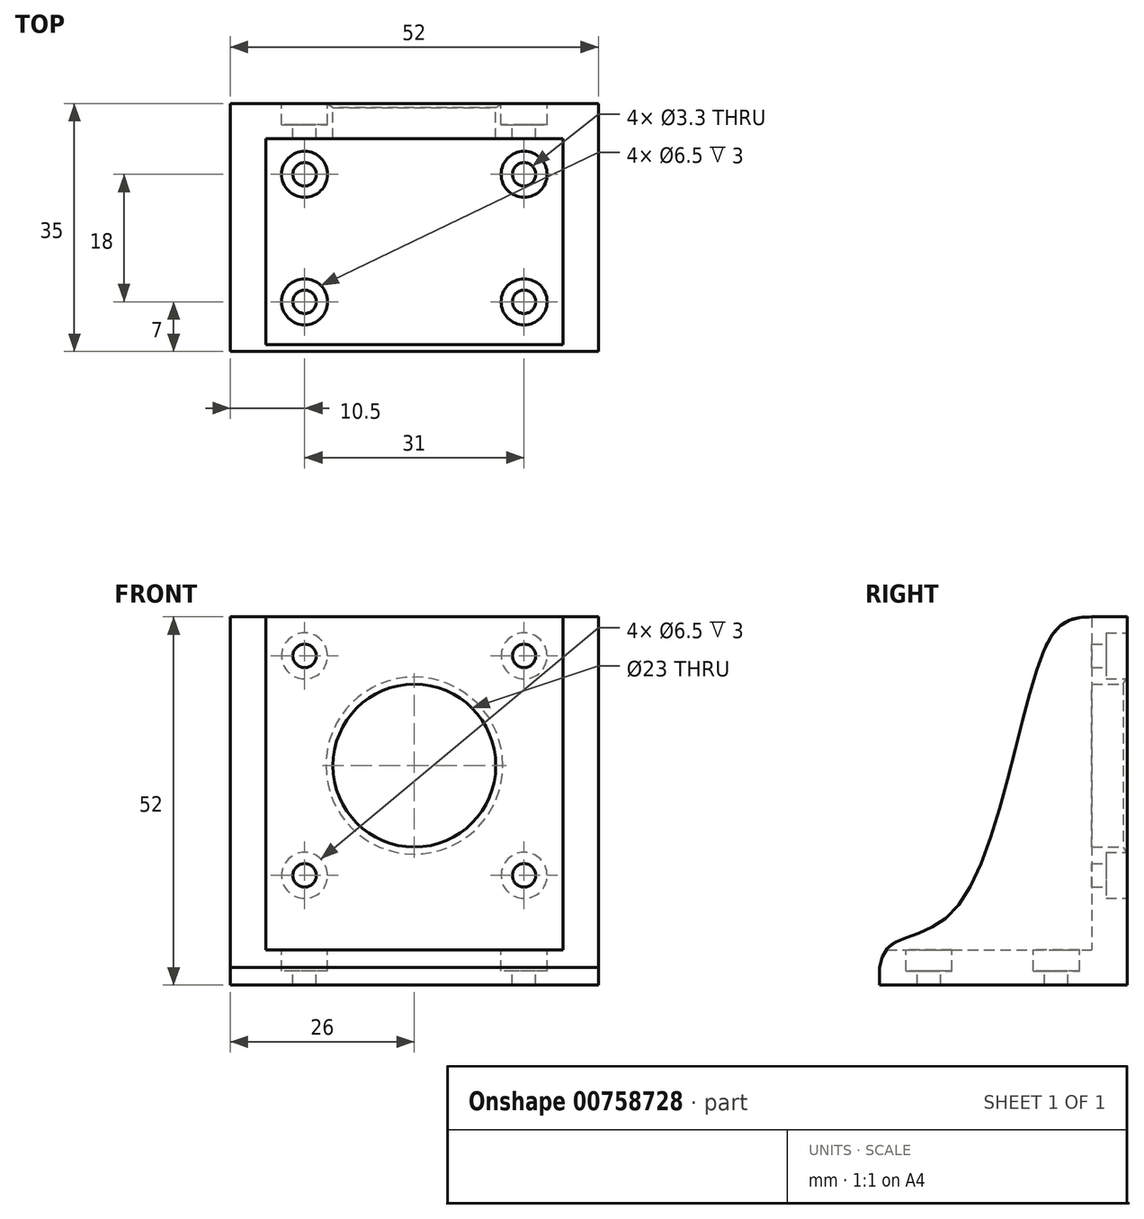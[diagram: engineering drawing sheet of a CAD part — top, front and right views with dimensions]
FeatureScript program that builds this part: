
annotation { "Feature Type Name" : "Feature", "Feature Type Description" : "" }
export const myFeature = defineFeature(function(context is Context, id is Id, definition is map)
    precondition{}
    {
        {
            var Q0;
            Q0=qCreatedBy(makeId("Front.planeOp"),FACE);
            var sketch = newSketch(context, id + "F0", { "sketchPlane" : qUnion([Q0])});
            skLineSegment(sketch, "E0.bottom", {"start": v(-26, 21) * mm, "end": v(0, 21) * mm});
            skLineSegment(sketch, "E0.top", {"start": v(-26, -31) * mm, "end": v(0, -31) * mm});
            skLineSegment(sketch, "E0.left", {"start": v(-26, 21) * mm, "end": v(-26, -31) * mm});
            skLineSegment(sketch, "E0.right", {"start": v(0, 21) * mm, "end": v(0, -31) * mm});
            skPoint(sketch, "E1", {"position": v(-15.5, 15.5) * mm});
            skPoint(sketch, "E2.MirrorP", {"position": v(-15.5, -15.5) * mm});
            skLineSegment(sketch, "E3.MirrorCS", {"start": v(-26, -21) * mm, "end": v(0, -21) * mm});
            skPoint(sketch, "E4", {"position": v(0, 0) * mm});
            skSolve(sketch);
        }
        {
            var Q0;
            Q0 = qSketchRegion(id + "F0", true);
            extrude(context, id + "F1", {"entities" : qUnion([Q0]), "depth" : 35 * mm, "offsetDistance" : 25 * mm});
        }
        {
            var Q0;
            Q0=makeQuery(id+"F1.opExtrude","SWEPT_FACE",FACE,{"disambiguationData":[OSD([sQuery(id+"F0.wireOp",EDGE,"E0.bottom")])]});
            var Q1;
            Q1=makeQuery(id+"F1.opExtrude","SWEPT_FACE",FACE,{"disambiguationData":[OSD([sQuery(id+"F0.wireOp",EDGE,"E0.right")])]});
            var Q2;
            Q2=makeQuery(id+"F1.opExtrude","CAP_FACE",FACE,{"disambiguationData":[OSD([sQuery(id+"F0.wireOp",EDGE,"E0.bottom"),sQuery(id+"F0.wireOp",EDGE,"E0.top"),sQuery(id+"F0.wireOp",EDGE,"E0.left"),sQuery(id+"F0.wireOp",EDGE,"E0.right")])],"isStart":false});
            shell(context, id + "F2", {"entities" : qUnion([Q0, Q1, Q2]), "thickness" : 5 * mm});
        }
        {
            var Q0;
            Q0=sQuery(id+"F0.wireOp",VERTEX,"E1");
            var Q1;
            Q1=sQuery(id+"F0.wireOp",VERTEX,"E2.MirrorP");
            var Q2;
            Q2=makeQuery(id+"F1.opExtrude","SWEPT_BODY",BODY,{"disambiguationData":[OSD([sQuery(id+"F0.wireOp",EDGE,"E0.bottom"),sQuery(id+"F0.wireOp",EDGE,"E0.top"),sQuery(id+"F0.wireOp",EDGE,"E0.left"),sQuery(id+"F0.wireOp",EDGE,"E0.right")])]});
            hole(context, id + "F3", {"style" : HoleStyle.C_BORE, "endStyle" : HoleEndStyle.THROUGH, "oppositeDirection" : true, "standardTappedOrClearance" : lookupTablePath({ "standard" : "ISO", "fit" : "Normal", "size" : "M3", "type" : "Clearance" }), "standardBlindInLast" : lookupTablePath({ "fit" : "Standard", "standard" : "ISO", "size" : "M3", "type" : "Clearance" }), "holeDiameter" : 3.3 * mm, "cBoreDiameter" : 6.5 * mm, "cBoreDepth" : 3 * mm, "majorDiameter" : 5 * mm, "isTappedThrough" : true, "tappedDepth" : 12 * mm, "tapClearance" : 3, "locations" : qUnion([Q0, Q1]), "scope" : qUnion([Q2])});
        }
        {
            var Q0;
            Q0=makeQuery(id+"F1.opExtrude","SWEPT_BODY",BODY,{"disambiguationData":[OSD([sQuery(id+"F0.wireOp",EDGE,"E0.bottom"),sQuery(id+"F0.wireOp",EDGE,"E0.top"),sQuery(id+"F0.wireOp",EDGE,"E0.left"),sQuery(id+"F0.wireOp",EDGE,"E0.right")])]});
            var Q1;
            Q1=qCreatedBy(makeId("Right.planeOp"),FACE);
            mirror(context, id + "F4", {"operationType" : NewBodyOperationType.ADD, "entities" : qUnion([Q0]), "mirrorPlane" : qUnion([Q1])});
        }
        {
            var Q0;
            Q0=sQuery(id+"F0.wireOp",VERTEX,"E4");
            var Q1;
            Q1=makeQuery(id+"F1.opExtrude","SWEPT_BODY",BODY,{"disambiguationData":[OSD([sQuery(id+"F0.wireOp",EDGE,"E0.bottom"),sQuery(id+"F0.wireOp",EDGE,"E0.top"),sQuery(id+"F0.wireOp",EDGE,"E0.left"),sQuery(id+"F0.wireOp",EDGE,"E0.right")])]});
            hole(context, id + "F5", {"style" : HoleStyle.C_SINK, "endStyle" : HoleEndStyle.THROUGH, "oppositeDirection" : true, "holeDiameter" : 23 * mm, "cSinkDiameter" : 25 * mm, "cSinkAngle" : 120 * degree, "majorDiameter" : 5 * mm, "isTappedThrough" : true, "tappedDepth" : 12 * mm, "tapClearance" : 3, "locations" : qUnion([Q0]), "scope" : qUnion([Q1])});
        }
        {
            var Q0;
            Q0=makeQuery(id+"F1.opExtrude","SWEPT_FACE",FACE,{"disambiguationData":[OSD([sQuery(id+"F0.wireOp",EDGE,"E0.left")])]});
            var sketch = newSketch(context, id + "F6", { "sketchPlane" : qUnion([Q0])});
            skPoint(sketch, "E5.0", {"position": v(35, 21) * mm});
            skPoint(sketch, "E6.0", {"position": v(5, 21) * mm});
            skPoint(sketch, "E7.0", {"position": v(35, -26) * mm});
            skLineSegment(sketch, "E8", {"start": v(5, 21) * mm, "end": v(35, 21) * mm});
            skLineSegment(sketch, "E9", {"start": v(35.17, -31.63) * mm, "end": v(35, 21) * mm});
            skFitSpline(sketch, "E10", {"points": [v(5, 21) * mm, v(11.25, 17.34) * mm, v(24.13, -20.1) * mm, v(33.73, -25.66) * mm, v(35.17, -31.63) * mm], "startDerivative": vector(45.26, 0) * mm, "endDerivative": vector(-0.24, -36.11) * mm});
            skSolve(sketch);
        }
        {
            var Q0;
            {var subQ0=sQuery(id+"F6.wireOp",EDGE,"E8");Q0=makeQuery(id+"F6.imprint","IMPRINT",FACE,{"disambiguationData":[TD([[makeQuery(id+"F6.imprint","IMPRINT",EDGE,{"derivedFrom":subQ0}),1.0]])]});}
            extrude(context, id + "F7", {"entities" : qUnion([Q0]), "operationType" : NewBodyOperationType.REMOVE, "endBound" : BoundingType.THROUGH_ALL, "oppositeDirection" : true, "depth" : 25 * mm, "offsetDistance" : 25 * mm});
        }
        {
            var Q0;
            {var subQ0=makeQuery(id+"F2.opShell","OFFSET_FACE",FACE,{"disambiguationData":[OSD([sQuery(id+"F0.wireOp",EDGE,"E0.top")])]});Q0=makeQuery(id+"F4.boolean.opBoolean","MERGE",FACE,{"derivedFrom":[subQ0,makeQuery(id+"F4.opPattern","COPY",FACE,{"derivedFrom":subQ0,"instanceName":"1"})]});}
            var sketch = newSketch(context, id + "F8", { "sketchPlane" : qUnion([Q0])});
            skPoint(sketch, "E11", {"position": v(-15.5, -10) * mm});
            skPoint(sketch, "E12", {"position": v(15.5, -10) * mm});
            skPoint(sketch, "E13", {"position": v(-15.5, -28) * mm});
            skPoint(sketch, "E14", {"position": v(15.5, -28) * mm});
            skLineSegment(sketch, "E15", {"start": v(-15.5, -10) * mm, "end": v(15.5, -10) * mm, "construction": true});
            skLineSegment(sketch, "E16", {"start": v(15.5, -28) * mm, "end": v(15.5, -10) * mm, "construction": true});
            skLineSegment(sketch, "E17", {"start": v(-15.5, -10) * mm, "end": v(-15.5, -28) * mm, "construction": true});
            skLineSegment(sketch, "E18", {"start": v(15.5, -28) * mm, "end": v(-15.5, -28) * mm, "construction": true});
            skSolve(sketch);
        }
        {
            var Q0;
            Q0=sQuery(id+"F8.wireOp",VERTEX,"E11");
            var Q1;
            Q1=sQuery(id+"F8.wireOp",VERTEX,"E12");
            var Q2;
            Q2=sQuery(id+"F8.wireOp",VERTEX,"E14");
            var Q3;
            Q3=sQuery(id+"F8.wireOp",VERTEX,"E13");
            var Q4;
            Q4=makeQuery(id+"F1.opExtrude","SWEPT_BODY",BODY,{"disambiguationData":[OSD([sQuery(id+"F0.wireOp",EDGE,"E0.bottom"),sQuery(id+"F0.wireOp",EDGE,"E0.top"),sQuery(id+"F0.wireOp",EDGE,"E0.left"),sQuery(id+"F0.wireOp",EDGE,"E0.right")])]});
            hole(context, id + "F9", {"style" : HoleStyle.C_BORE, "endStyle" : HoleEndStyle.THROUGH, "holeDiameter" : 3.3 * mm, "cBoreDiameter" : 6.5 * mm, "cBoreDepth" : 3 * mm, "majorDiameter" : 5 * mm, "isTappedThrough" : true, "tappedDepth" : 12 * mm, "tapClearance" : 3, "locations" : qUnion([Q0, Q1, Q2, Q3]), "scope" : qUnion([Q4])});
        }
    });
